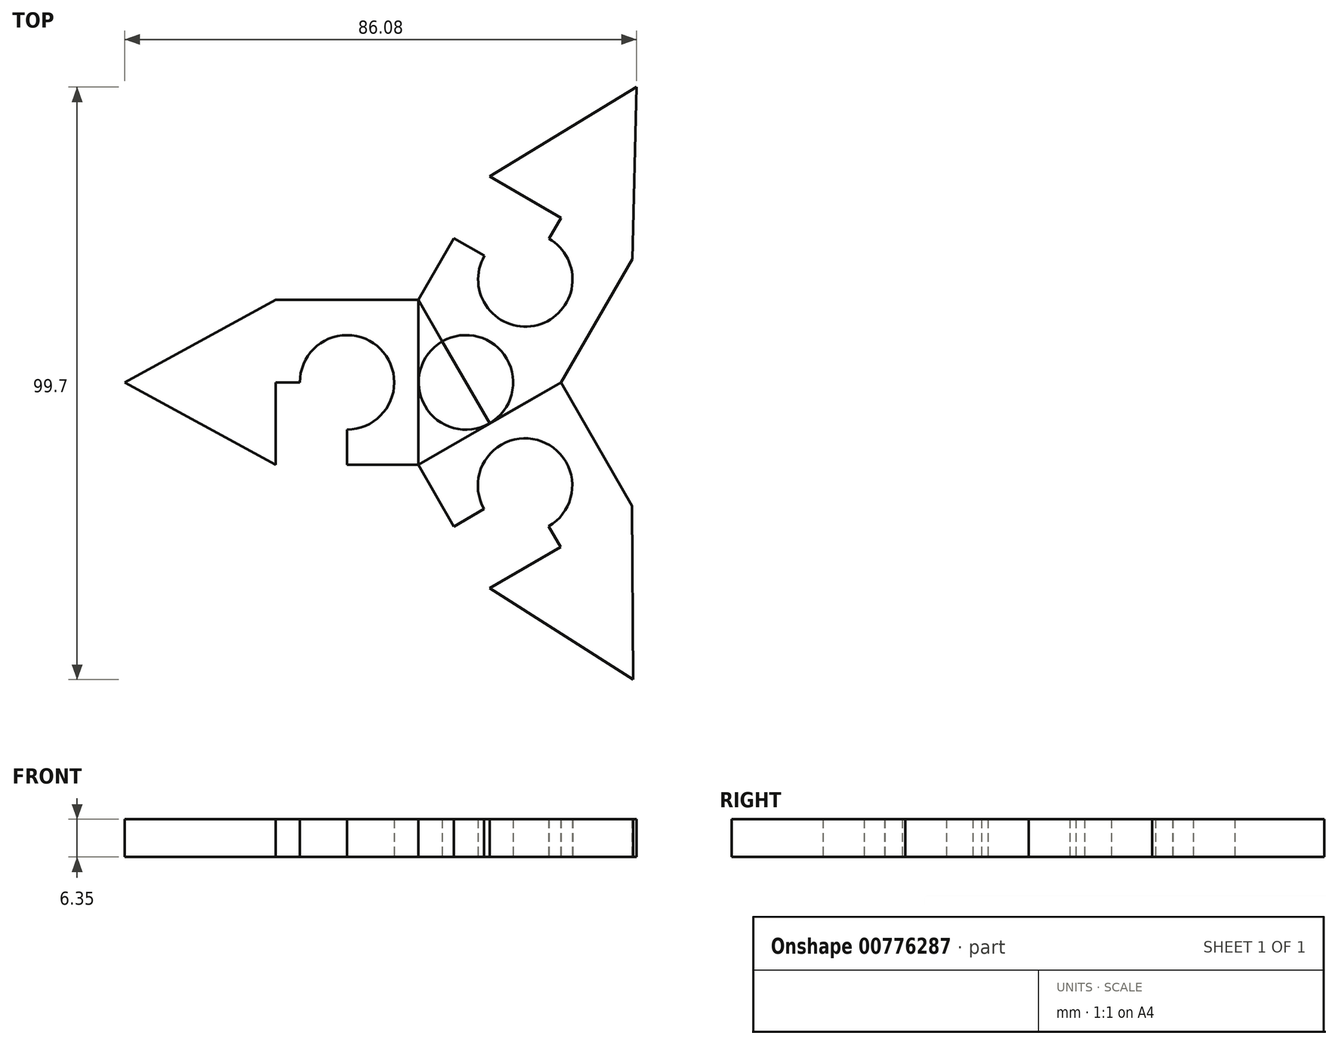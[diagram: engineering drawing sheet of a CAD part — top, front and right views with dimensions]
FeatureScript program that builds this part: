
annotation { "Feature Type Name" : "Feature", "Feature Type Description" : "" }
export const myFeature = defineFeature(function(context is Context, id is Id, definition is map)
    precondition{}
    {
        {
            var Q0;
            Q0=qCreatedBy(makeId("Top.planeOp"),FACE);
            var sketch = newSketch(context, id + "F0", { "sketchPlane" : qUnion([Q0])});
            skLineSegment(sketch, "E0", {"start": v(0, 0) * mm, "end": v(-8.01, 0) * mm});
            skLineSegment(sketch, "E1.0", {"start": v(-8.01, -13.88) * mm, "end": v(-8.01, 13.88) * mm});
            skLineSegment(sketch, "E1.1", {"start": v(-8.01, 13.88) * mm, "end": v(16.02, 0) * mm});
            skLineSegment(sketch, "E1.2", {"start": v(16.02, 0) * mm, "end": v(-8.01, -13.88) * mm});
            skPoint(sketch, "E1.0.midPoint", {"position": v(-8.01, 0) * mm});
            skLineSegment(sketch, "E2", {"start": v(0, 0) * mm, "end": v(-7.95, 0) * mm});
            skCircle(sketch, "E3", {"center": v(0, 0) * mm, "radius": 7.95 * mm});
            skLineSegment(sketch, "E4", {"start": v(-8.01, 13.88) * mm, "end": v(3.98, -6.89) * mm});
            skLineSegment(sketch, "E5", {"start": v(3.98, -6.89) * mm, "end": v(16.02, 0) * mm});
            skLineSegment(sketch, "E6", {"start": v(16.02, 0) * mm, "end": v(28, 20.76) * mm});
            skLineSegment(sketch, "E7", {"start": v(-8.01, 13.88) * mm, "end": v(3.97, 34.64) * mm});
            skLineSegment(sketch, "E8", {"start": v(3.97, 34.64) * mm, "end": v(28, 20.76) * mm});
            skLineSegment(sketch, "E9", {"start": v(-8.01, 13.88) * mm, "end": v(-31.99, 13.88) * mm});
            skLineSegment(sketch, "E10", {"start": v(-8.01, -13.88) * mm, "end": v(-31.99, -13.88) * mm});
            skLineSegment(sketch, "E11", {"start": v(-31.99, -13.88) * mm, "end": v(-31.99, 13.88) * mm});
            skLineSegment(sketch, "E12", {"start": v(-8.01, -13.88) * mm, "end": v(3.97, -34.64) * mm});
            skLineSegment(sketch, "E13", {"start": v(16.02, 0) * mm, "end": v(27.92, -20.8) * mm});
            skLineSegment(sketch, "E14", {"start": v(27.92, -20.8) * mm, "end": v(3.97, -34.64) * mm});
            skLineSegment(sketch, "E15", {"start": v(3.97, -34.64) * mm, "end": v(15.95, -27.72) * mm});
            skLineSegment(sketch, "E16", {"start": v(3.97, -34.64) * mm, "end": v(-2.02, -24.26) * mm});
            skLineSegment(sketch, "E17", {"start": v(-2.02, -24.26) * mm, "end": v(9.95, -17.35) * mm});
            skLineSegment(sketch, "E18", {"start": v(9.95, -17.35) * mm, "end": v(15.95, -27.72) * mm});
            skCircle(sketch, "E19", {"center": v(9.95, -17.35) * mm, "radius": 7.94 * mm});
            skLineSegment(sketch, "E20", {"start": v(3.97, 34.64) * mm, "end": v(16, 27.7) * mm});
            skLineSegment(sketch, "E21", {"start": v(3.97, 34.64) * mm, "end": v(-2.02, 24.26) * mm});
            skLineSegment(sketch, "E22", {"start": v(16, 27.7) * mm, "end": v(10, 17.32) * mm});
            skLineSegment(sketch, "E23", {"start": v(10, 17.32) * mm, "end": v(-2.02, 24.26) * mm});
            skCircle(sketch, "E24", {"center": v(10, 17.32) * mm, "radius": 7.94 * mm});
            skLineSegment(sketch, "E25", {"start": v(-31.99, 0) * mm, "end": v(-31.99, -13.88) * mm});
            skLineSegment(sketch, "E26", {"start": v(-20, -13.88) * mm, "end": v(-20, 0) * mm});
            skLineSegment(sketch, "E27", {"start": v(-20, 0) * mm, "end": v(-31.99, 0) * mm});
            skCircle(sketch, "E28", {"center": v(-20, 0) * mm, "radius": 7.94 * mm});
            skLineSegment(sketch, "E29", {"start": v(16, 27.7) * mm, "end": v(28.69, 49.69) * mm});
            skLineSegment(sketch, "E30", {"start": v(28.69, 49.69) * mm, "end": v(3.97, 34.64) * mm});
            skLineSegment(sketch, "E31", {"start": v(28.69, 49.69) * mm, "end": v(28, 20.76) * mm});
            skLineSegment(sketch, "E32", {"start": v(-31.99, 0) * mm, "end": v(-57.4, 0) * mm});
            skLineSegment(sketch, "E33", {"start": v(-57.4, 0) * mm, "end": v(-31.99, 13.88) * mm});
            skLineSegment(sketch, "E34", {"start": v(-31.99, -13.88) * mm, "end": v(-57.4, 0) * mm});
            skLineSegment(sketch, "E35", {"start": v(15.95, -27.72) * mm, "end": v(28.12, -50) * mm});
            skLineSegment(sketch, "E36", {"start": v(28.12, -50) * mm, "end": v(27.92, -20.8) * mm});
            skLineSegment(sketch, "E37", {"start": v(28.12, -50) * mm, "end": v(3.97, -34.64) * mm});
            skSolve(sketch);
        }
        {
            var Q0;
            Q0=makeQuery(id+"F0.imprint","IMPRINT",FACE,{"disambiguationData":[TD([[makeQuery(id+"F0.imprint","IMPRINT",EDGE,{"derivedFrom":sQuery(id+"F0.wireOp",EDGE,"E11")}),1.0]])]});
            var Q1;
            Q1=makeQuery(id+"F0.imprint","IMPRINT",FACE,{"disambiguationData":[TD([[makeQuery(id+"F0.imprint","IMPRINT",EDGE,{"derivedFrom":sQuery(id+"F0.wireOp",EDGE,"E25")}),-1.0]])]});
            var Q2;
            {var subQ5=sQuery(id+"F0.wireOp",EDGE,"E25");Q2=makeQuery(id+"F0.imprint","IMPRINT",FACE,{"disambiguationData":[TD([[makeQuery(id+"F0.imprint","IMPRINT",EDGE,{"derivedFrom":subQ5}),1.0]])]});}
            var Q3;
            {var subQ6=sQuery(id+"F0.wireOp",EDGE,"E9");Q3=makeQuery(id+"F0.imprint","IMPRINT",FACE,{"disambiguationData":[TD([[makeQuery(id+"F0.imprint","IMPRINT",EDGE,{"derivedFrom":subQ6}),1.0]])]});}
            var Q4;
            {var subQ1=sQuery(id+"F0.wireOp",EDGE,"E0");Q4=makeQuery(id+"F0.imprint","IMPRINT",FACE,{"disambiguationData":[TD([[makeQuery(id+"F0.imprint","IMPRINT",EDGE,{"derivedFrom":subQ1}),1.0]])]});}
            var Q5;
            {var subQ0=sQuery(id+"F0.wireOp",EDGE,"E0");Q5=makeQuery(id+"F0.imprint","IMPRINT",FACE,{"disambiguationData":[TD([[makeQuery(id+"F0.imprint","IMPRINT",EDGE,{"derivedFrom":subQ0}),-1.0]])]});}
            var Q6;
            {var subQ0=sQuery(id+"F0.wireOp",EDGE,"E1.1");Q6=makeQuery(id+"F0.imprint","IMPRINT",FACE,{"disambiguationData":[TD([[makeQuery(id+"F0.imprint","IMPRINT",EDGE,{"derivedFrom":subQ0}),-1.0]])]});}
            var Q7;
            {var subQ5=sQuery(id+"F0.wireOp",EDGE,"E15");Q7=makeQuery(id+"F0.imprint","IMPRINT",FACE,{"disambiguationData":[TD([[makeQuery(id+"F0.imprint","IMPRINT",EDGE,{"derivedFrom":subQ5}),1.0]])]});}
            var Q8;
            Q8=makeQuery(id+"F0.imprint","IMPRINT",FACE,{"disambiguationData":[TD([[makeQuery(id+"F0.imprint","IMPRINT",EDGE,{"derivedFrom":sQuery(id+"F0.wireOp",EDGE,"E1.2")}),1.0]])]});
            var Q9;
            Q9=makeQuery(id+"F0.imprint","IMPRINT",FACE,{"disambiguationData":[TD([[makeQuery(id+"F0.imprint","IMPRINT",EDGE,{"derivedFrom":sQuery(id+"F0.wireOp",EDGE,"E14")}),1.0]])]});
            var Q10;
            Q10=makeQuery(id+"F0.imprint","IMPRINT",FACE,{"disambiguationData":[TD([[makeQuery(id+"F0.imprint","IMPRINT",EDGE,{"derivedFrom":sQuery(id+"F0.wireOp",EDGE,"E15")}),-1.0]])]});
            var Q11;
            Q11=makeQuery(id+"F0.imprint","IMPRINT",FACE,{"disambiguationData":[TD([[makeQuery(id+"F0.imprint","IMPRINT",EDGE,{"derivedFrom":sQuery(id+"F0.wireOp",EDGE,"E1.1")}),1.0]])]});
            var Q12;
            {var subQ1=sQuery(id+"F0.wireOp",EDGE,"E20");Q12=makeQuery(id+"F0.imprint","IMPRINT",FACE,{"disambiguationData":[TD([[makeQuery(id+"F0.imprint","IMPRINT",EDGE,{"derivedFrom":subQ1}),-1.0]])]});}
            var Q13;
            Q13=makeQuery(id+"F0.imprint","IMPRINT",FACE,{"disambiguationData":[TD([[makeQuery(id+"F0.imprint","IMPRINT",EDGE,{"derivedFrom":sQuery(id+"F0.wireOp",EDGE,"E20")}),1.0]])]});
            var Q14;
            Q14=makeQuery(id+"F0.imprint","IMPRINT",FACE,{"disambiguationData":[TD([[makeQuery(id+"F0.imprint","IMPRINT",EDGE,{"derivedFrom":sQuery(id+"F0.wireOp",EDGE,"E8")}),1.0]])]});
            extrude(context, id + "F1", {"entities" : qUnion([Q0, Q1, Q2, Q3, Q4, Q5, Q6, Q7, Q8, Q9, Q10, Q11, Q12, Q13, Q14]), "depth" : 6.35 * mm, "offsetDistance" : 25.4 * mm});
        }
    });
